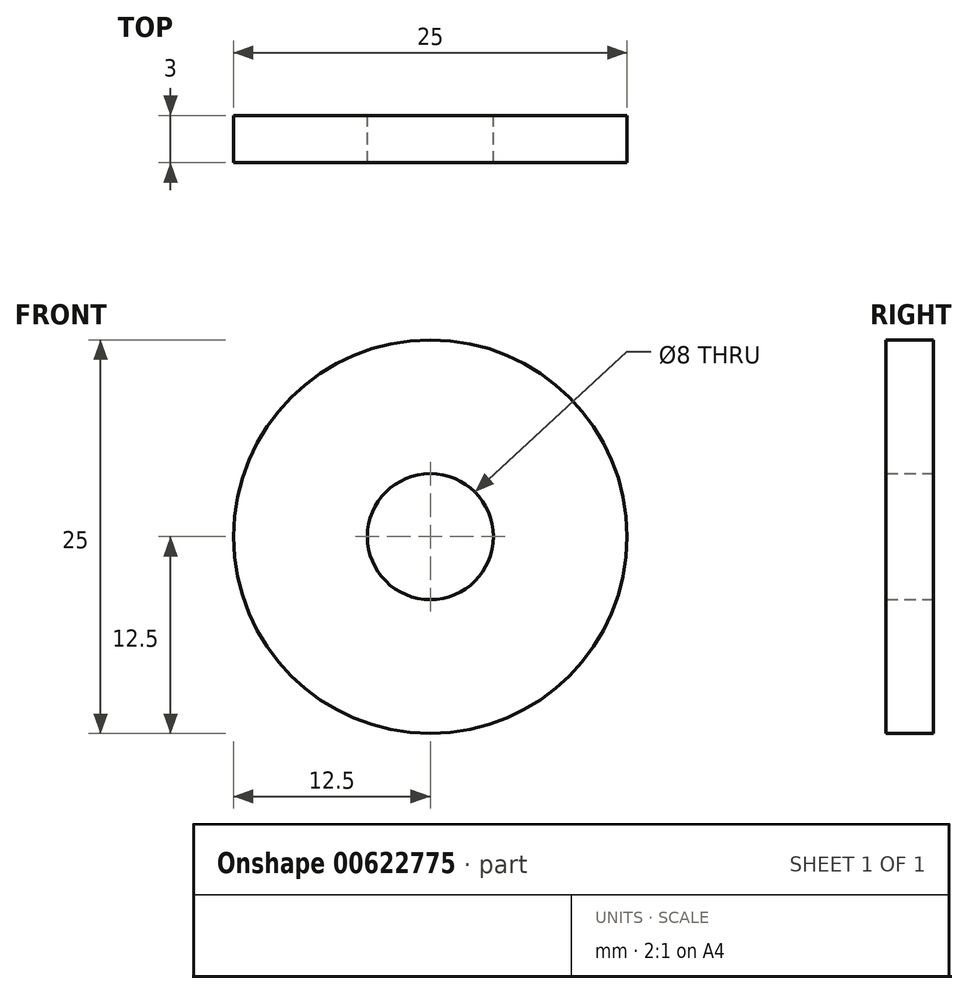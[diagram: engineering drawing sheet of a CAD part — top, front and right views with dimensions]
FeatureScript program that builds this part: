
annotation { "Feature Type Name" : "Feature", "Feature Type Description" : "" }
export const myFeature = defineFeature(function(context is Context, id is Id, definition is map)
    precondition{}
    {
        {
            var Q0;
            Q0=qCreatedBy(makeId("Front.planeOp"),FACE);
            var sketch = newSketch(context, id + "F0", { "sketchPlane" : qUnion([Q0])});
            skCircle(sketch, "E0", {"center": v(0, 0) * mm, "radius": 12.5 * mm});
            skCircle(sketch, "E1", {"center": v(0, 0) * mm, "radius": 4 * mm});
            skSolve(sketch);
        }
        {
            var Q0;
            Q0 = qSketchRegion(id + "F0", true);
            extrude(context, id + "F1", {"entities" : qUnion([Q0]), "depth" : 3 * mm, "offsetDistance" : 25 * mm});
        }
    });
